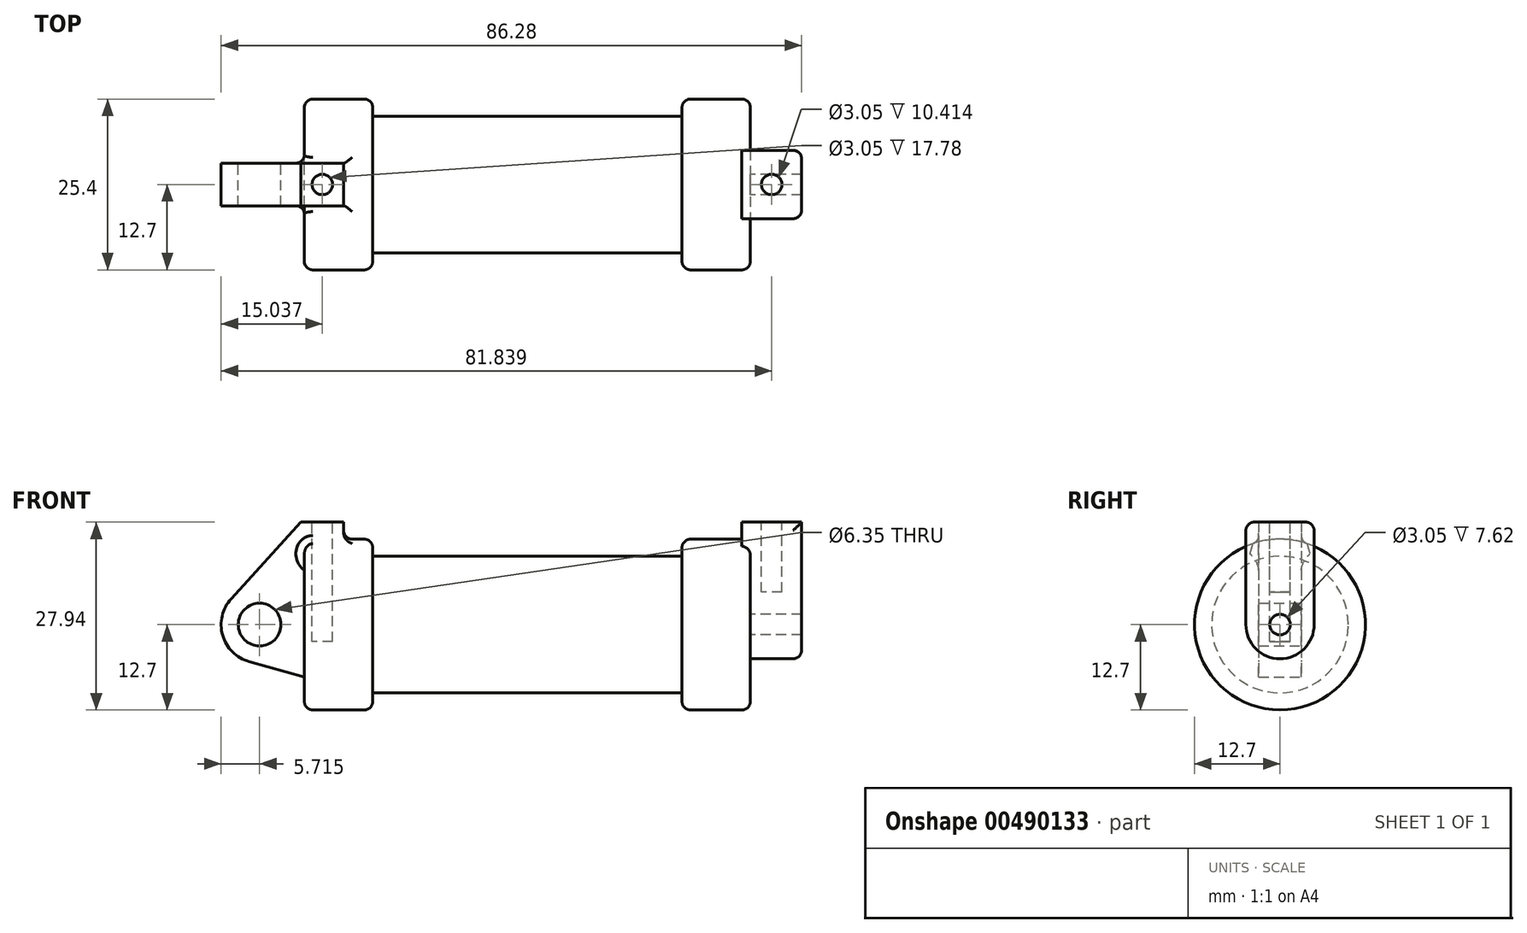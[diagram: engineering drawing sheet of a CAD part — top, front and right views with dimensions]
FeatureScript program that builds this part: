
annotation { "Feature Type Name" : "Feature", "Feature Type Description" : "" }
export const myFeature = defineFeature(function(context is Context, id is Id, definition is map)
    precondition{}
    {
        {
            var Q0;
            Q0=qCreatedBy(makeId("Front.planeOp"),FACE);
            var sketch = newSketch(context, id + "F0", { "sketchPlane" : qUnion([Q0])});
            skLineSegment(sketch, "E0", {"start": v(0, 0) * mm, "end": v(0, 12.7) * mm});
            skLineSegment(sketch, "E1", {"start": v(0, 12.7) * mm, "end": v(10.16, 12.7) * mm});
            skLineSegment(sketch, "E2", {"start": v(10.16, 12.7) * mm, "end": v(10.16, 10.16) * mm});
            skLineSegment(sketch, "E3", {"start": v(10.16, 10.16) * mm, "end": v(56.13, 10.16) * mm});
            skLineSegment(sketch, "E4", {"start": v(56.13, 10.16) * mm, "end": v(56.13, 12.7) * mm});
            skLineSegment(sketch, "E5", {"start": v(56.13, 12.7) * mm, "end": v(66.3, 12.7) * mm});
            skLineSegment(sketch, "E6", {"start": v(66.3, 12.7) * mm, "end": v(66.3, 0) * mm});
            skLineSegment(sketch, "E7", {"start": v(66.3, 0) * mm, "end": v(0, 0) * mm});
            skLineSegment(sketch, "E8", {"start": v(5.84, 15.24) * mm, "end": v(-0.5, 15.24) * mm});
            skLineSegment(sketch, "E9", {"start": v(-0.5, 15.24) * mm, "end": v(-10.88, 3.85) * mm});
            skLineSegment(sketch, "E10", {"start": v(0, 0) * mm, "end": v(-6.65, 0) * mm});
            skCircle(sketch, "E11", {"center": v(-6.65, 0) * mm, "radius": 5.72 * mm});
            skCircle(sketch, "E12", {"center": v(-6.65, 0) * mm, "radius": 3.18 * mm});
            skLineSegment(sketch, "E13", {"start": v(5.84, 15.24) * mm, "end": v(5.84, -9.4) * mm});
            skLineSegment(sketch, "E14", {"start": v(5.84, -9.4) * mm, "end": v(-8.18, -5.5) * mm});
            skSolve(sketch);
        }
        {
            var Q0;
            {var subQ0=sQuery(id+"F0.wireOp",EDGE,"E2");Q0=makeQuery(id+"F0.imprint","IMPRINT",FACE,{"disambiguationData":[TD([[makeQuery(id+"F0.imprint","IMPRINT",EDGE,{"derivedFrom":subQ0}),-1.0]])]});}
            var Q1;
            {var subQ0=sQuery(id+"F0.wireOp",EDGE,"E0");Q1=makeQuery(id+"F0.imprint","IMPRINT",FACE,{"disambiguationData":[TD([[makeQuery(id+"F0.imprint","IMPRINT",EDGE,{"derivedFrom":subQ0}),-1.0]])]});}
            var Q2;
            Q2=sQuery(id+"F0.wireOp",EDGE,"E10");
            revolve(context, id + "F1", {"entities" : qUnion([Q0, Q1]), "axis" : qUnion([Q2]), "revolveType" : RevolveType.FULL});
        }
        {
            var Q0;
            {var subQ0=sQuery(id+"F0.wireOp",EDGE,"E14");Q0=makeQuery(id+"F0.imprint","IMPRINT",FACE,{"disambiguationData":[TD([[makeQuery(id+"F0.imprint","IMPRINT",EDGE,{"derivedFrom":subQ0}),-1.0]])]});}
            var Q1;
            {var subQ5=sQuery(id+"F0.wireOp",EDGE,"E12");Q1=makeQuery(id+"F0.imprint","IMPRINT",FACE,{"disambiguationData":[TD([[makeQuery(id+"F0.imprint","IMPRINT",EDGE,{"derivedFrom":subQ5}),-1.0]])]});}
            var Q2;
            {var subQ1=sQuery(id+"F0.wireOp",EDGE,"E0");Q2=makeQuery(id+"F0.imprint","IMPRINT",FACE,{"disambiguationData":[TD([[makeQuery(id+"F0.imprint","IMPRINT",EDGE,{"derivedFrom":subQ1}),1.0]])]});}
            var Q3;
            {var subQ0=sQuery(id+"F0.wireOp",EDGE,"E0");Q3=makeQuery(id+"F0.imprint","IMPRINT",FACE,{"disambiguationData":[TD([[makeQuery(id+"F0.imprint","IMPRINT",EDGE,{"derivedFrom":subQ0}),-1.0]])]});}
            extrude(context, id + "F2", {"entities" : qUnion([Q0, Q1, Q2, Q3]), "operationType" : NewBodyOperationType.ADD, "endBound" : BoundingType.SYMMETRIC, "depth" : 6.35 * mm});
        }
        {
            var Q0;
            Q0=makeQuery(id+"F1.opRevolve","SWEPT_FACE",FACE,{"disambiguationData":[OSD([sQuery(id+"F0.wireOp",EDGE,"E6")])]});
            var sketch = newSketch(context, id + "F3", { "sketchPlane" : qUnion([Q0])});
            skCircle(sketch, "E15", {"center": v(0, 0) * mm, "radius": 1.52 * mm});
            skCircle(sketch, "E16", {"center": v(0, 0) * mm, "radius": 5.08 * mm});
            skLineSegment(sketch, "E17", {"start": v(-5.08, 0) * mm, "end": v(-5.08, 15.24) * mm});
            skLineSegment(sketch, "E18", {"start": v(5.08, 0) * mm, "end": v(5.08, 15.24) * mm});
            skLineSegment(sketch, "E19", {"start": v(-5.08, 15.24) * mm, "end": v(5.08, 15.24) * mm});
            skSolve(sketch);
        }
        {
            var Q0;
            {var subQ0=sQuery(id+"F3.wireOp",EDGE,"E19");Q0=makeQuery(id+"F3.imprint","IMPRINT",FACE,{"disambiguationData":[TD([[makeQuery(id+"F3.imprint","IMPRINT",EDGE,{"derivedFrom":subQ0}),-1.0]])]});}
            var Q1;
            {var subQ0=sQuery(id+"F3.wireOp",EDGE,"E17");var subQ1=sQuery(id+"F3.wireOp",EDGE,"E16");var subQ2=makeQuery(id+"F3.imprint","INTERSECT",VERTEX,{"derivedFrom":[subQ1,subQ0]});Q1=makeQuery(id+"F3.imprint","IMPRINT",FACE,{"disambiguationData":[TD([[makeQuery(id+"F3.imprint","IMPRINT",EDGE,{"disambiguationData":[TD([[subQ2,1.0]])],"derivedFrom":subQ1}),-1.0]])]});}
            var Q2;
            Q2=makeQuery(id+"F3.imprint","IMPRINT",FACE,{"disambiguationData":[TD([[makeQuery(id+"F3.imprint","IMPRINT",EDGE,{"derivedFrom":sQuery(id+"F3.wireOp",EDGE,"E15")}),-1.0]])]});
            extrude(context, id + "F4", {"entities" : qUnion([Q0, Q1, Q2]), "operationType" : NewBodyOperationType.ADD, "depth" : 7.62 * mm, "hasSecondDirection" : true, "secondDirectionOppositeDirection" : true, "secondDirectionDepth" : 1.27 * mm});
        }
        {
            var Q0;
            Q0=makeQuery(id+"F2.opExtrude","SWEPT_FACE",FACE,{"disambiguationData":[OSD([sQuery(id+"F0.wireOp",EDGE,"E8")])]});
            var sketch = newSketch(context, id + "F5", { "sketchPlane" : qUnion([Q0])});
            skLineSegment(sketch, "E20", {"start": v(65.02, 0) * mm, "end": v(73.91, 0) * mm, "construction": true});
            skCircle(sketch, "E21", {"center": v(69.47, 0) * mm, "radius": 1.52 * mm});
            skLineSegment(sketch, "E22", {"start": v(-0.5, 0) * mm, "end": v(5.84, 0) * mm, "construction": true});
            skCircle(sketch, "E23", {"center": v(2.67, 0) * mm, "radius": 1.52 * mm});
            skSolve(sketch);
        }
        {
            var Q0;
            Q0=makeQuery(id+"F5.imprint","IMPRINT",FACE,{"disambiguationData":[TD([[makeQuery(id+"F5.imprint","IMPRINT",EDGE,{"derivedFrom":sQuery(id+"F5.wireOp",EDGE,"E21")}),1.0]])]});
            extrude(context, id + "F6", {"entities" : qUnion([Q0]), "operationType" : NewBodyOperationType.REMOVE, "oppositeDirection" : true, "depth" : 10.4 * mm});
        }
        {
            var Q0;
            Q0=makeQuery(id+"F1.opRevolve","SWEPT_EDGE",EDGE,{"disambiguationData":[OSD([sQuery(id+"F0.wireOp",EDGE,"E0"),sQuery(id+"F0.wireOp",EDGE,"E1")])]});
            var Q1;
            Q1=makeQuery(id+"F1.opRevolve","SWEPT_FACE",FACE,{"disambiguationData":[OSD([sQuery(id+"F0.wireOp",EDGE,"E1")])]});
            var Q2;
            Q2=makeQuery(id+"F1.opRevolve","SWEPT_EDGE",EDGE,{"disambiguationData":[OSD([sQuery(id+"F0.wireOp",EDGE,"E1"),sQuery(id+"F0.wireOp",EDGE,"E2")])]});
            var Q3;
            Q3=makeQuery(id+"F1.opRevolve","SWEPT_EDGE",EDGE,{"disambiguationData":[OSD([sQuery(id+"F0.wireOp",EDGE,"E4"),sQuery(id+"F0.wireOp",EDGE,"E5")])]});
            var Q4;
            Q4=makeQuery(id+"F1.opRevolve","SWEPT_EDGE",EDGE,{"disambiguationData":[OSD([sQuery(id+"F0.wireOp",EDGE,"E5"),sQuery(id+"F0.wireOp",EDGE,"E6")])]});
            fillet(context, id + "F7", {"entities" : qUnion([Q0, Q1, Q2, Q3, Q4]), "radius" : 1.27 * mm, "tangentPropagation" : true, "allowEdgeOverflow" : false});
        }
        {
            var Q0;
            Q0=makeQuery(id+"F4.opExtrude","CAP_EDGE",EDGE,{"disambiguationData":[OSD([sQuery(id+"F3.wireOp",EDGE,"E17")])],"isStart":false});
            var Q1;
            Q1=makeQuery(id+"F4.opExtrude","CAP_EDGE",EDGE,{"disambiguationData":[OSD([sQuery(id+"F3.wireOp",EDGE,"E16")])],"isStart":false});
            var Q2;
            Q2=makeQuery(id+"F4.opExtrude","CAP_EDGE",EDGE,{"disambiguationData":[OSD([sQuery(id+"F3.wireOp",EDGE,"E18")])],"isStart":false});
            var Q3;
            Q3=makeQuery(id+"F4.opExtrude","SWEPT_EDGE",EDGE,{"disambiguationData":[OSD([sQuery(id+"F3.wireOp",EDGE,"E17"),sQuery(id+"F3.wireOp",EDGE,"E19")])]});
            var Q4;
            Q4=makeQuery(id+"F4.opExtrude","SWEPT_EDGE",EDGE,{"disambiguationData":[OSD([sQuery(id+"F3.wireOp",EDGE,"E18"),sQuery(id+"F3.wireOp",EDGE,"E19")])]});
            fillet(context, id + "F8", {"entities" : qUnion([Q0, Q1, Q2, Q3, Q4]), "radius" : 1.27 * mm, "tangentPropagation" : true, "allowEdgeOverflow" : false});
        }
        {
            var Q0;
            Q0=makeQuery(id+"F5.imprint","IMPRINT",FACE,{"disambiguationData":[TD([[makeQuery(id+"F5.imprint","IMPRINT",EDGE,{"derivedFrom":sQuery(id+"F5.wireOp",EDGE,"E23")}),1.0]])]});
            extrude(context, id + "F9", {"entities" : qUnion([Q0]), "operationType" : NewBodyOperationType.REMOVE, "oppositeDirection" : true, "depth" : 17.78 * mm});
        }
    });
